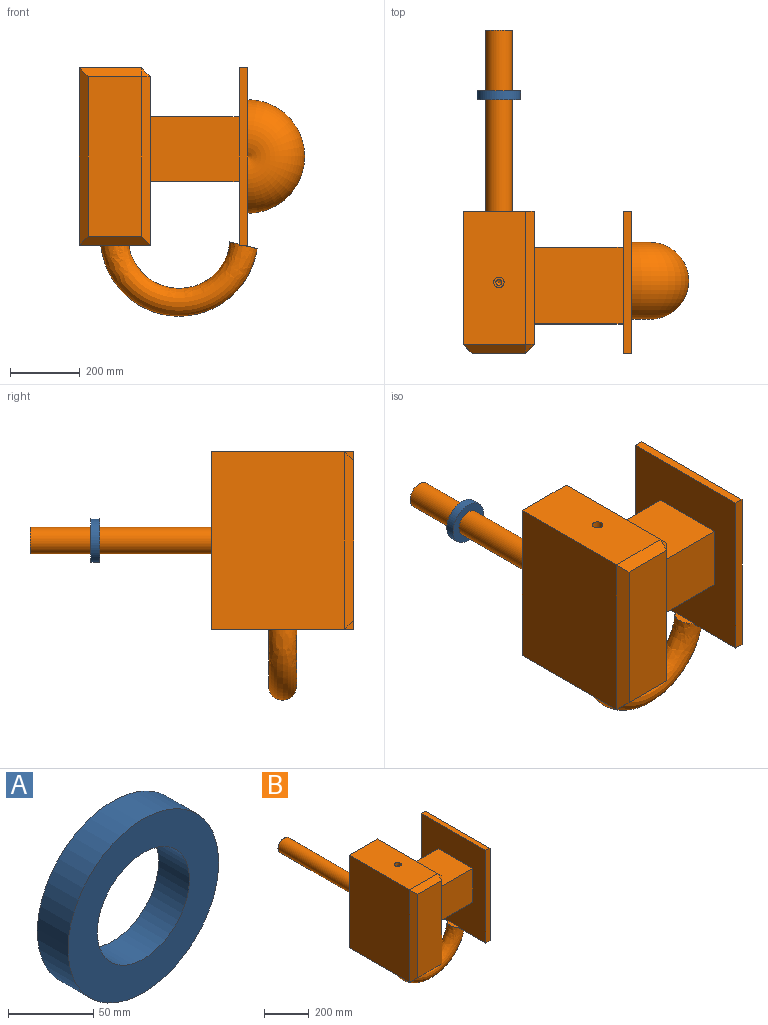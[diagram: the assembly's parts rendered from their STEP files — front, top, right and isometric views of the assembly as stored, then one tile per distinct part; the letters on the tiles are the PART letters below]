
ASSEMBLY  parts=2 mates=1
PART A: 4 faces, bbox 124.5x25.4x124.5 mm
  f0: cylinder r=38.1mm len=76.2mm, axis (0,1,0), area 6080.5mm2, adj f2,f3
  f1: cylinder r=62.27mm len=124.54mm, axis (0,1,0), area 9938.2mm2, adj f2,f3
  f2: plane 124.54x124.54mm, normal (0,-1,0), area 7622.1mm2, adj f0,f1
  f3: plane 124.54x124.54mm, normal (0,1,0), area 7622.1mm2, adj f0,f1
PART B: 32 faces, bbox 645.2x924.7x875.1 mm
  f0: plane 508x406.4mm, normal (1,0,0), area 146313.8mm2, adj f11,f12,f13,f14,f16
  f1: plane 457.2x152.4mm, normal (0,-1,0), area 69677.3mm2, adj f21,f22,f24,f25
  f2: plane 482.6x381mm, normal (1,0,0), area 143094.4mm2, adj f3,f6,f7,f8,f9,f10,f20,f21
  f3: plane 508x203.2mm, normal (0,1,0), area 98342.7mm2, adj f2,f4,f5,f6,f20,f30
  f4: plane 508x381mm, normal (-1,0,0), area 193548mm2, adj f3,f5,f6,f24
  f5: plane 381x177.8mm, normal (0,0,1), area 67027.3mm2, adj f3,f4,f20,f25,f28
  f6: plane 381x203.2mm, normal (0,0,-1), area 72353.8mm2, adj f2,f3,f4,f19,f22
  f7: plane 254x218.77mm, normal (0,0,-1), area 55567.9mm2, adj f2,f8,f10,f15
  f8: plane 254x186.39mm, normal (0,1,0), area 47342.3mm2, adj f2,f7,f9,f15
  f9: plane 254x218.77mm, normal (0,0,1), area 55567.9mm2, adj f2,f8,f10,f15
  f10: plane 254x186.39mm, normal (0,-1,0), area 47342.3mm2, adj f2,f7,f9,f15
  f11: plane 406.4x25.4mm, normal (0,0,1), area 10322.6mm2, adj f0,f12,f14,f15
  f12: plane 508x25.4mm, normal (0,-1,0), area 12903.2mm2, adj f0,f11,f13,f15
  f13: plane 406.51x25.51mm, normal (0,0,-1), area 9319.9mm2, adj f0,f12,f14,f15,f17,f19
  f14: plane 508x25.4mm, normal (0,1,0), area 12903.2mm2, adj f0,f11,f13,f15
  f15: plane 508.02x406.42mm, normal (-1,0,0), area 165438.6mm2, adj f7,f8,f9,f10,f11,f12,f13,f14
  f16: torus R=52.65mm, axis (0,-1,0), area 141818.3mm2, adj f0
  f17: plane 80.31x39mm, normal (0.24,0,0.97), area 2532.7mm2, adj f13,f19
  f18: plane 75.93x26.3mm, normal (0.24,0,0.97), area 1501.5mm2, adj f15,f19
  f19: bspline ~447.46x376.57mm, area 135475.7mm2, adj f6,f13,f15,f17,f18
  f20: plane 381x25.4mm, normal (0.71,0,0.71), area 13685.9mm2, adj f2,f3,f5,f23
  f21: plane 482.6x25.4mm, normal (0.71,-0.71,0), area 16879.3mm2, adj f1,f2,f22,f23
  f22: plane 203.2x25.4mm, normal (0,-0.71,-0.71), area 6386.8mm2, adj f1,f6,f21,f24
  f23: plane 25.4x25.4mm, normal (0.58,-0.58,0.58), area 558.7mm2, adj f20,f21,f25
  f24: plane 508x25.4mm, normal (-0.71,-0.71,0), area 17335.5mm2, adj f1,f4,f22,f25
  f25: plane 177.8x25.4mm, normal (0,-0.71,0.71), area 5930.6mm2, adj f1,f5,f23,f24
  f26: cylinder r=8.33mm len=234.95mm, axis (0,0,1), area 12302.6mm2, adj f27,f29
  f27: plane 30.16x30.16mm, normal (0,0,1), area 496.3mm2, adj f26,f28
  f28: cylinder r=15.08mm len=30.16mm, axis (0,0,1), area 1805.1mm2, adj f5,f27
  f29: cone r=0mm half-angle=59deg, axis (0,0,1), area 254.5mm2, adj f26
  f30: cylinder r=38.1mm len=518.16mm, axis (0,-1,0), area 124042mm2, adj f3,f31
  f31: plane 76.2x76.2mm, normal (0,1,0), area 4560.4mm2, adj f30
PLACE A t=(567.06,197.14,222.98)mm
PLACE B t=(567.06,-351.39,222.98)mm
MATE slider B.f30 <-> A.f1  axis (0,1,0) through (567.06,369.97,222.98)mm
